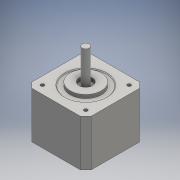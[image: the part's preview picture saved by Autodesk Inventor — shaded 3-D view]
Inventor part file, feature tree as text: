
AUTODESK INVENTOR PART (.ipt)
format: ipt  version: 2016 (Build 200138000, 138)  size: 242,688 bytes
history: native  units: mm
features: sketch x6, extrude x5, chamfer x1
ambient origin geometry x8: Origin, YZ Plane, XZ Plane, XY Plane, X Axis, Y Axis, Z Axis, Center Point
bodies: Solid1 (feature_tree), Body (feature_tree)
feature tree (12):
  extrude  "Raised"  Depth=42.0mm
  extrude  "Axle"  Depth=27.0mm
  extrude  "Face Indent"  Depth=27.0mm
  chamfer  "Indent Chamf"  Distance=2.5mm
  extrude  "Power Base"  Depth=2.5mm
  extrude  "Extrusion7"  Depth=2.5mm
  sketch  "Sketch1"  dims[d0=42.0mm d1=42.0mm]
  sketch  "Sketch2"  dims[d2=27.0mm d3=27.0mm]
  sketch  "Sketch3"  dims[d4=27.0mm d5=27.0mm]
  sketch  "Sketch4"  dims[d18=34.367532mm]
  sketch  "Sketch5"  dims[d19=30.75mm]
  sketch  "Sketch6"  dims[d20=30.75mm d21=2.5mm d22=2.5mm d23=2.5mm d24=2.5mm d25=33.0mm d26=0.0mm d27=22.0mm d28=2.0mm d29=0.0mm d30=5.0mm d31=22.0mm d32=0.0mm d33=9.5mm d34=30.0mm d35=2.5mm d36=0.0mm d37=0.5mm d38=2.0mm d39=45.0deg d40=8.0mm d41=11.25mm d42=16.0mm d43=3.75mm d44=0.0mm d45=6.4mm d48=1.0mm d49=1.0mm d50=1.0mm d51=0.5mm d52=4.0mm d53=4.0mm d59=1.571429mm d60=0.5mm d61=1.571429mm d62=0.5mm d63=1.571429mm d64=0.5mm d65=1.571429mm d66=0.5mm d67=1.571429mm d68=0.5mm d69=1.571429mm d70=0.5mm d71=0.5mm d72=0.5mm d73=0.5mm d74=0.5mm d75=0.5mm d76=0.5mm d77=0.5mm d78=0.5mm d79=0.5mm d80=0.5mm d81=2.571429mm d82=3.2mm d83=1.0mm d84=3.2mm d85=3.2mm d86=2.25mm d87=0.0mm]
